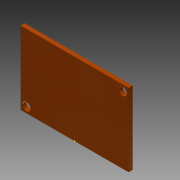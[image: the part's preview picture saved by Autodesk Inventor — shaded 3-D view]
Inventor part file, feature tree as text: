
AUTODESK INVENTOR PART (.ipt)
format: ipt  version: 2015 (Build 190159000, 159)  size: 99,328 bytes
history: native  units: mm
features: sketch x3, extrude x2
ambient origin geometry x8: Origin, YZ Plane, XZ Plane, XY Plane, X Axis, Y Axis, Z Axis, Center Point
bodies: Solid1 (feature_tree)
feature tree (5):
  sketch  "Sketch1"  dims[d0=46.5mm d1=31.42mm]
  extrude  "Extrusion1"  Depth=31.42mm
  extrude  "Extrusion2"  Depth=3.5mm
  sketch  "Sketch2"  dims[d2=3.5mm d3=3.5mm]
  sketch  "Sketch3"  dims[d4=2.5mm d5=2.5mm d6=2.5mm d7=2.5mm d8=1.7mm d9=0.0mm d10=13.25mm d11=0.0mm]
